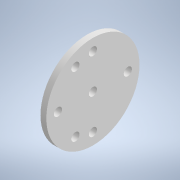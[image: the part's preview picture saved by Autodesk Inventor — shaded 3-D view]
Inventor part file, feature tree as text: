
AUTODESK INVENTOR PART (.ipt)
format: ipt  version: 2021 (Build 250183000, 183)  size: 116,224 bytes
history: native  units: mm
features: extrude x2, sketch x2
ambient origin geometry x8: Origin, YZ Plane, XZ Plane, XY Plane, X Axis, Y Axis, Z Axis, Center Point
bodies: Solid1 (feature_tree)
feature tree (4):
  extrude  "Extrusion1"  Depth=5.0mm TaperAngle=0.0deg
  extrude  "Extrusion2"  Depth=40.0mm
  sketch  "Sketch1"  dims[d0=80.0mm d1=5.0mm d2=0.0mm]
  sketch  "Sketch2"  dims[d3=7.0mm d4=30.0mm d5=7.0mm d6=40.0mm d8=360.0deg d10=30.0mm d12=360.0deg d14=0.0mm d15=0.0mm]
